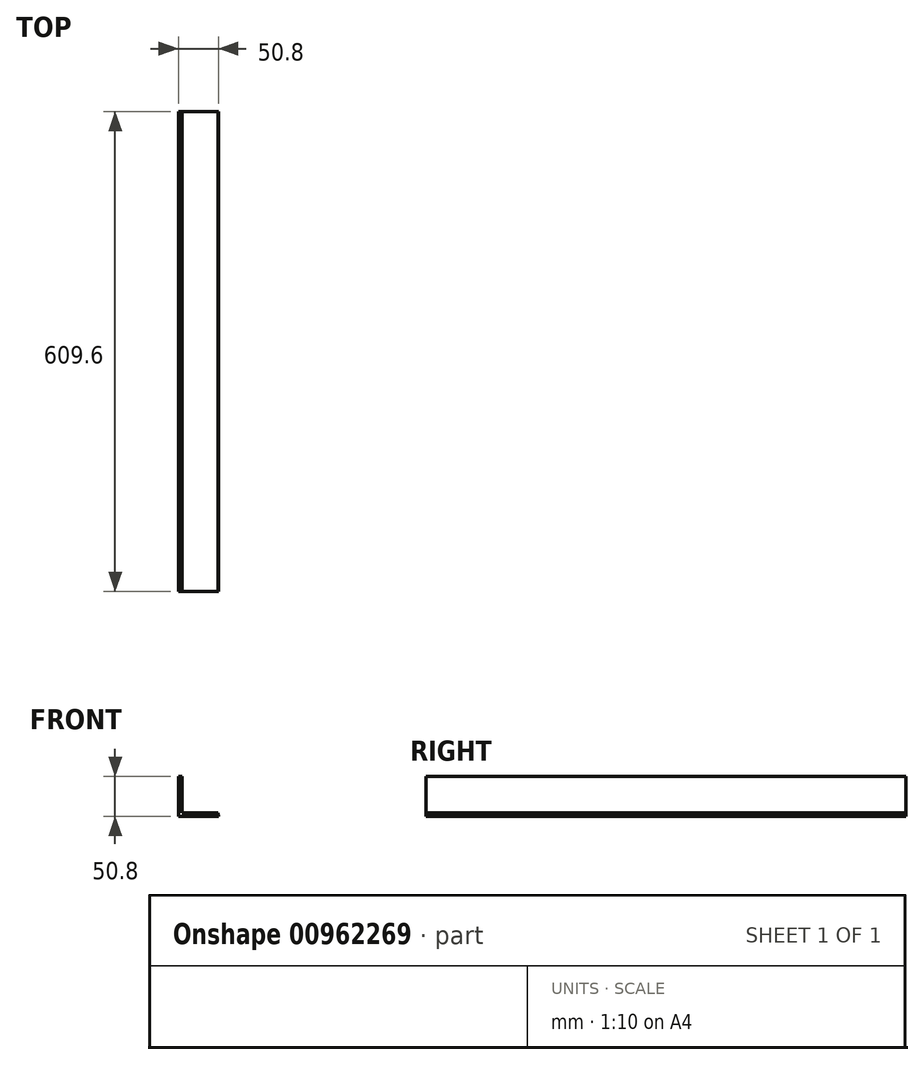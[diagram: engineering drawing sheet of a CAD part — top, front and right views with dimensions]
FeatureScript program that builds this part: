
annotation { "Feature Type Name" : "Feature", "Feature Type Description" : "" }
export const myFeature = defineFeature(function(context is Context, id is Id, definition is map)
    precondition{}
    {
        {
            var Q0;
            Q0=qCreatedBy(makeId("Front.planeOp"),FACE);
            var sketch = newSketch(context, id + "F0", { "sketchPlane" : qUnion([Q0])});
            skLineSegment(sketch, "E0", {"start": v(0, 50.8) * mm, "end": v(0, 0) * mm});
            skLineSegment(sketch, "E1", {"start": v(0, 0) * mm, "end": v(50.8, 0) * mm});
            skLineSegment(sketch, "E2", {"start": v(0, 50.8) * mm, "end": v(4.76, 50.8) * mm});
            skLineSegment(sketch, "E3", {"start": v(4.76, 50.8) * mm, "end": v(4.76, 4.76) * mm});
            skLineSegment(sketch, "E4", {"start": v(4.76, 4.76) * mm, "end": v(50.74, 4.76) * mm});
            skLineSegment(sketch, "E5", {"start": v(50.74, 4.76) * mm, "end": v(50.8, 0) * mm});
            skSolve(sketch);
        }
        {
            var Q0;
            Q0=makeQuery(id+"F0.imprint","IMPRINT",FACE,{"disambiguationData":[TD([[makeQuery(id+"F0.imprint","IMPRINT",EDGE,{"derivedFrom":sQuery(id+"F0.wireOp",EDGE,"E0")}),1.0]])]});
            extrude(context, id + "F1", {"entities" : qUnion([Q0]), "depth" : 609.6 * mm, "offsetDistance" : 25.4 * mm});
        }
    });
